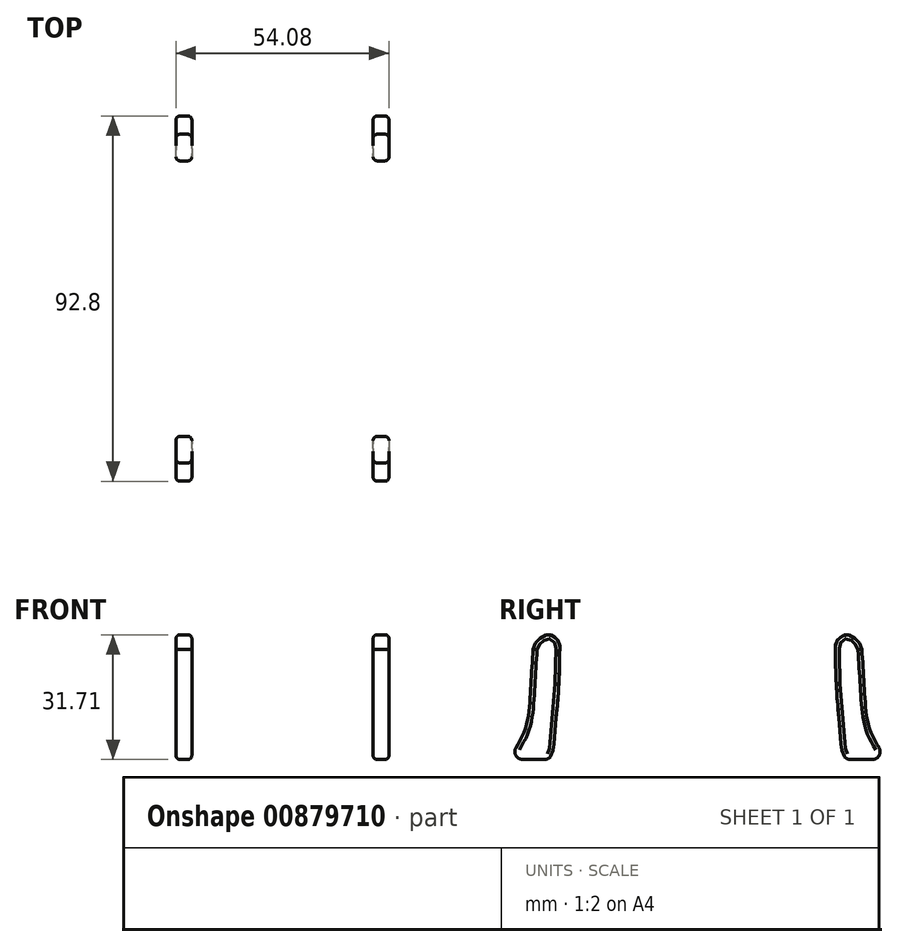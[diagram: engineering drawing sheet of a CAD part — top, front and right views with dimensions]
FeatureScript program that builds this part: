
annotation { "Feature Type Name" : "Feature", "Feature Type Description" : "" }
export const myFeature = defineFeature(function(context is Context, id is Id, definition is map)
    precondition{}
    {
        {
            var Q0;
            Q0=qCreatedBy(makeId("Right.planeOp"),FACE);
            var sketch = newSketch(context, id + "F0", { "sketchPlane" : qUnion([Q0])});
            skFitSpline(sketch, "E0", {"points": [v(41.76, 28.04) * mm, v(42.4, 17.71) * mm, v(44.03, 6.98) * mm, v(46.64, 1.77) * mm, v(46.4, 0) * mm], "startDerivative": vector(2.12, -32.11) * mm, "endDerivative": vector(-4.6, -12.44) * mm});
            skFitSpline(sketch, "E1", {"points": [v(41.76, 28.04) * mm, v(40.78, 30.08) * mm, v(37.69, 31.7) * mm, v(35.33, 30) * mm, v(35, 28.04) * mm, v(35.33, 17.63) * mm, v(36.3, 6.32) * mm, v(36.96, 1.36) * mm, v(38.1, 0) * mm], "startDerivative": vector(-6.83, 22.41) * mm, "endDerivative": vector(16.14, -13.75) * mm});
            skLineSegment(sketch, "E2", {"start": v(46.4, 0) * mm, "end": v(38.1, 0) * mm});
            skSolve(sketch);
        }
        {
            var Q0;
            Q0=makeQuery(id+"F0.imprint","IMPRINT",FACE,{"disambiguationData":[TD([[makeQuery(id+"F0.imprint","IMPRINT",EDGE,{"derivedFrom":sQuery(id+"F0.wireOp",EDGE,"E0")}),-1.0]])]});
            extrude(context, id + "F1", {"entities" : qUnion([Q0]), "depth" : 4 * mm, "offsetDistance" : 25.4 * mm});
        }
        {
            var Q0;
            Q0=makeQuery(id+"F1.opExtrude","SWEPT_EDGE",EDGE,{"disambiguationData":[OSD([sQuery(id+"F0.wireOp",EDGE,"E0"),sQuery(id+"F0.wireOp",EDGE,"E2")])]});
            var Q1;
            Q1=makeQuery(id+"F1.opExtrude","SWEPT_EDGE",EDGE,{"disambiguationData":[OSD([sQuery(id+"F0.wireOp",EDGE,"E1"),sQuery(id+"F0.wireOp",EDGE,"E2")])]});
            fillet(context, id + "F2", {"entities" : qUnion([Q0, Q1]), "radius" : 2 * mm, "tangentPropagation" : true, "allowEdgeOverflow" : false});
        }
        {
            var Q0;
            Q0=qCreatedBy(makeId("Front.planeOp"),FACE);
            var sketch = newSketch(context, id + "F3", { "sketchPlane" : qUnion([Q0])});
            skPoint(sketch, "E3", {"position": v(-22.2, 15.33) * mm});
            skPoint(sketch, "E4", {"position": v(0.84, 14.55) * mm});
            skSolve(sketch);
        }
        {
            var Q0;
            Q0=makeQuery(id+"F1.opExtrude","SWEPT_BODY",BODY,{"disambiguationData":[OSD([sQuery(id+"F0.wireOp",EDGE,"E0"),sQuery(id+"F0.wireOp",EDGE,"E1"),sQuery(id+"F0.wireOp",EDGE,"E2")])]});
            var Q1;
            Q1=sQuery(id+"F3.wireOp",VERTEX,"E3");
            var Q2;
            Q2=sQuery(id+"F3.wireOp",VERTEX,"E4");
            transform(context, id + "F4", {"entities" : qUnion([Q0]), "transformType" : TransformType.TRANSLATION_ENTITY, "oppositeDirectionEntity" : false, "transformLine" : qUnion([Q1, Q2]), "makeCopy" : false});
        }
        {
            var Q0;
            Q0=makeQuery(id+"F1.opExtrude","CAP_EDGE",EDGE,{"disambiguationData":[OSD([sQuery(id+"F0.wireOp",EDGE,"E1")])],"isStart":true});
            var Q1;
            Q1=makeQuery(id+"F1.opExtrude","CAP_EDGE",EDGE,{"disambiguationData":[OSD([sQuery(id+"F0.wireOp",EDGE,"E0")])],"isStart":true});
            var Q2;
            {var subQ0=sQuery(id+"F0.wireOp",EDGE,"E2");var subQ1=sQuery(id+"F0.wireOp",EDGE,"E0");Q2=makeQuery(id+"F2.opFillet","BLEND_EDGE",EDGE,{"blendedFrom":[makeQuery(id+"F1.opExtrude","SWEPT_EDGE",EDGE,{"disambiguationData":[OSD([subQ1,subQ0])]}),makeQuery(id+"F1.opExtrude","CAP_FACE",FACE,{"disambiguationData":[OSD([subQ1,sQuery(id+"F0.wireOp",EDGE,"E1"),subQ0])],"isStart":true})],"blendedInto":[makeQuery(id+"F1.opExtrude","CAP_FACE",FACE,{"disambiguationData":[OSD([subQ1,sQuery(id+"F0.wireOp",EDGE,"E1"),subQ0])],"isStart":true})]});}
            var Q3;
            {var subQ0=sQuery(id+"F0.wireOp",EDGE,"E2");var subQ1=sQuery(id+"F0.wireOp",EDGE,"E1");Q3=makeQuery(id+"F2.opFillet","BLEND_EDGE",EDGE,{"blendedFrom":[makeQuery(id+"F1.opExtrude","SWEPT_EDGE",EDGE,{"disambiguationData":[OSD([subQ1,subQ0])]}),makeQuery(id+"F1.opExtrude","CAP_FACE",FACE,{"disambiguationData":[OSD([sQuery(id+"F0.wireOp",EDGE,"E0"),subQ1,subQ0])],"isStart":true})],"blendedInto":[makeQuery(id+"F1.opExtrude","CAP_FACE",FACE,{"disambiguationData":[OSD([sQuery(id+"F0.wireOp",EDGE,"E0"),subQ1,subQ0])],"isStart":true})]});}
            var Q4;
            Q4=makeQuery(id+"F1.opExtrude","CAP_EDGE",EDGE,{"disambiguationData":[OSD([sQuery(id+"F0.wireOp",EDGE,"E1")])],"isStart":false});
            var Q5;
            Q5=makeQuery(id+"F1.opExtrude","CAP_EDGE",EDGE,{"disambiguationData":[OSD([sQuery(id+"F0.wireOp",EDGE,"E0")])],"isStart":false});
            var Q6;
            Q6=makeQuery(id+"F1.opExtrude","CAP_EDGE",EDGE,{"disambiguationData":[OSD([sQuery(id+"F0.wireOp",EDGE,"E2")])],"isStart":false});
            var Q7;
            {var subQ0=sQuery(id+"F0.wireOp",EDGE,"E2");var subQ1=sQuery(id+"F0.wireOp",EDGE,"E0");Q7=makeQuery(id+"F2.opFillet","BLEND_EDGE",EDGE,{"blendedFrom":[makeQuery(id+"F1.opExtrude","SWEPT_EDGE",EDGE,{"disambiguationData":[OSD([subQ1,subQ0])]}),makeQuery(id+"F1.opExtrude","CAP_FACE",FACE,{"disambiguationData":[OSD([subQ1,sQuery(id+"F0.wireOp",EDGE,"E1"),subQ0])],"isStart":false})],"blendedInto":[makeQuery(id+"F1.opExtrude","CAP_FACE",FACE,{"disambiguationData":[OSD([subQ1,sQuery(id+"F0.wireOp",EDGE,"E1"),subQ0])],"isStart":false})]});}
            var Q8;
            Q8=makeQuery(id+"F1.opExtrude","CAP_EDGE",EDGE,{"disambiguationData":[OSD([sQuery(id+"F0.wireOp",EDGE,"E2")])],"isStart":true});
            fillet(context, id + "F5", {"entities" : qUnion([Q0, Q1, Q2, Q3, Q4, Q5, Q6, Q7, Q8]), "radius" : 1 * mm, "tangentPropagation" : true, "allowEdgeOverflow" : false});
        }
        {
            var Q0;
            Q0=makeQuery(id+"F1.opExtrude","SWEPT_BODY",BODY,{"disambiguationData":[OSD([sQuery(id+"F0.wireOp",EDGE,"E0"),sQuery(id+"F0.wireOp",EDGE,"E1"),sQuery(id+"F0.wireOp",EDGE,"E2")])]});
            var Q1;
            Q1=qCreatedBy(makeId("Right.planeOp"),FACE);
            mirror(context, id + "F6", {"entities" : qUnion([Q0]), "mirrorPlane" : qUnion([Q1])});
        }
        {
            var Q0;
            Q0=makeQuery(id+"F1.opExtrude","SWEPT_BODY",BODY,{"disambiguationData":[OSD([sQuery(id+"F0.wireOp",EDGE,"E0"),sQuery(id+"F0.wireOp",EDGE,"E1"),sQuery(id+"F0.wireOp",EDGE,"E2")])]});
            var Q1;
            Q1=makeQuery(id+"F6.opPattern","COPY",BODY,{"derivedFrom":makeQuery(id+"F1.opExtrude","SWEPT_BODY",BODY,{"disambiguationData":[OSD([sQuery(id+"F0.wireOp",EDGE,"E0"),sQuery(id+"F0.wireOp",EDGE,"E1"),sQuery(id+"F0.wireOp",EDGE,"E2")])]}),"instanceName":"1"});
            var Q2;
            Q2=qCreatedBy(makeId("Front.planeOp"),FACE);
            mirror(context, id + "F7", {"entities" : qUnion([Q0, Q1]), "mirrorPlane" : qUnion([Q2])});
        }
    });
